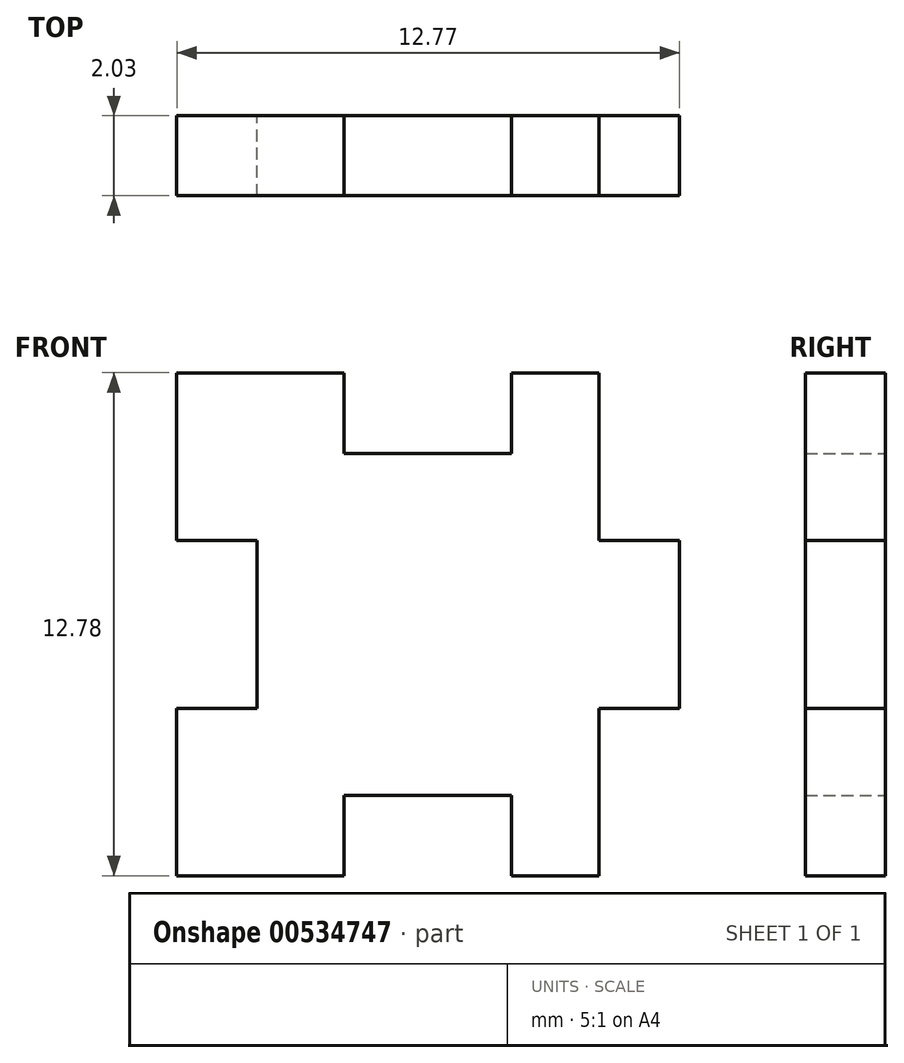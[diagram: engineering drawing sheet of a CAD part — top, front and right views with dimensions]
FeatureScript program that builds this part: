
annotation { "Feature Type Name" : "Feature", "Feature Type Description" : "" }
export const myFeature = defineFeature(function(context is Context, id is Id, definition is map)
    precondition{}
    {
        {
            var Q0;
            Q0=qCreatedBy(makeId("Front.planeOp"),FACE);
            var sketch = newSketch(context, id + "F0", { "sketchPlane" : qUnion([Q0])});
            skLineSegment(sketch, "E0", {"start": v(-10.99, 26.89) * mm, "end": v(-10.99, 29.02) * mm});
            skLineSegment(sketch, "E1", {"start": v(-10.99, 29.02) * mm, "end": v(-13.03, 29.02) * mm});
            skLineSegment(sketch, "E2", {"start": v(-13.03, 29.02) * mm, "end": v(-13.03, 33.28) * mm});
            skLineSegment(sketch, "E3", {"start": v(-13.03, 33.28) * mm, "end": v(-8.78, 33.28) * mm});
            skLineSegment(sketch, "E4", {"start": v(-8.78, 33.28) * mm, "end": v(-8.78, 31.23) * mm});
            skLineSegment(sketch, "E5", {"start": v(-8.78, 31.23) * mm, "end": v(-4.53, 31.23) * mm});
            skLineSegment(sketch, "E6", {"start": v(-4.53, 31.23) * mm, "end": v(-4.53, 33.28) * mm});
            skLineSegment(sketch, "E7", {"start": v(-4.53, 33.28) * mm, "end": v(-2.3, 33.28) * mm});
            skLineSegment(sketch, "E8", {"start": v(-2.3, 33.28) * mm, "end": v(-2.3, 29.02) * mm});
            skLineSegment(sketch, "E9", {"start": v(-2.3, 29.02) * mm, "end": v(-0.26, 29.02) * mm});
            skLineSegment(sketch, "E10", {"start": v(-10.99, 26.89) * mm, "end": v(8.72, 26.89) * mm, "construction": true});
            skLineSegment(sketch, "E11.MirrorCS", {"start": v(-2.3, 24.76) * mm, "end": v(-0.26, 24.76) * mm});
            skLineSegment(sketch, "E12.MirrorCS", {"start": v(-2.3, 20.5) * mm, "end": v(-2.3, 24.76) * mm});
            skLineSegment(sketch, "E13.MirrorCS", {"start": v(-4.53, 20.5) * mm, "end": v(-2.3, 20.5) * mm});
            skLineSegment(sketch, "E14.MirrorCS", {"start": v(-4.53, 22.55) * mm, "end": v(-4.53, 20.5) * mm});
            skLineSegment(sketch, "E15.MirrorCS", {"start": v(-8.78, 22.55) * mm, "end": v(-4.53, 22.55) * mm});
            skLineSegment(sketch, "E16.MirrorCS", {"start": v(-8.78, 20.5) * mm, "end": v(-8.78, 22.55) * mm});
            skLineSegment(sketch, "E17.MirrorCS", {"start": v(-13.03, 20.5) * mm, "end": v(-8.78, 20.5) * mm});
            skLineSegment(sketch, "E18.MirrorCS", {"start": v(-13.03, 24.76) * mm, "end": v(-13.03, 20.5) * mm});
            skLineSegment(sketch, "E19.MirrorCS", {"start": v(-10.99, 24.76) * mm, "end": v(-13.03, 24.76) * mm});
            skLineSegment(sketch, "E20.MirrorCS", {"start": v(-10.99, 26.89) * mm, "end": v(-10.99, 24.76) * mm});
            skLineSegment(sketch, "E21", {"start": v(-0.26, 29.02) * mm, "end": v(-0.26, 24.76) * mm});
            skSolve(sketch);
        }
        {
            var Q0;
            Q0=makeQuery(id+"F0.imprint","IMPRINT",FACE,{"disambiguationData":[TD([[makeQuery(id+"F0.imprint","IMPRINT",EDGE,{"derivedFrom":sQuery(id+"F0.wireOp",EDGE,"E0")}),-1.0]])]});
            extrude(context, id + "F1", {"entities" : qUnion([Q0]), "depth" : 2.03 * mm, "offsetDistance" : 25.4 * mm});
        }
        {
            var Q0;
            Q0=qCreatedBy(makeId("Front.planeOp"),FACE);
            cPlane(context, id + "F2", {"entities" : qUnion([Q0]), "cplaneType" : CPlaneType.OFFSET, "offset" : 4.06 * mm, "width" : 152.4 * mm, "height" : 152.4 * mm});
        }
        {
            var Q0;
            Q0=qCreatedBy(id+"F2.planeOp",FACE);
            var sketch = newSketch(context, id + "F3", { "sketchPlane" : qUnion([Q0])});
            skText(sketch, "E22", { "text": "U", "fontName": "OpenSans-Regular.ttf"});
            const initialGuessF3  = {"E22": [-0.0093, 0.02415, 1, 0, 0.00571]};
            skSetInitialGuess(sketch, initialGuessF3);
            skSolve(sketch);
        }
        {
            var Q0;
            Q0 = qSketchRegion(id + "F3", true);
            extrude(context, id + "F4", {"entities" : qUnion([Q0]), "operationType" : NewBodyOperationType.REMOVE, "oppositeDirection" : true, "depth" : 0.5 * mm, "offsetDistance" : 25.4 * mm});
        }
    });
